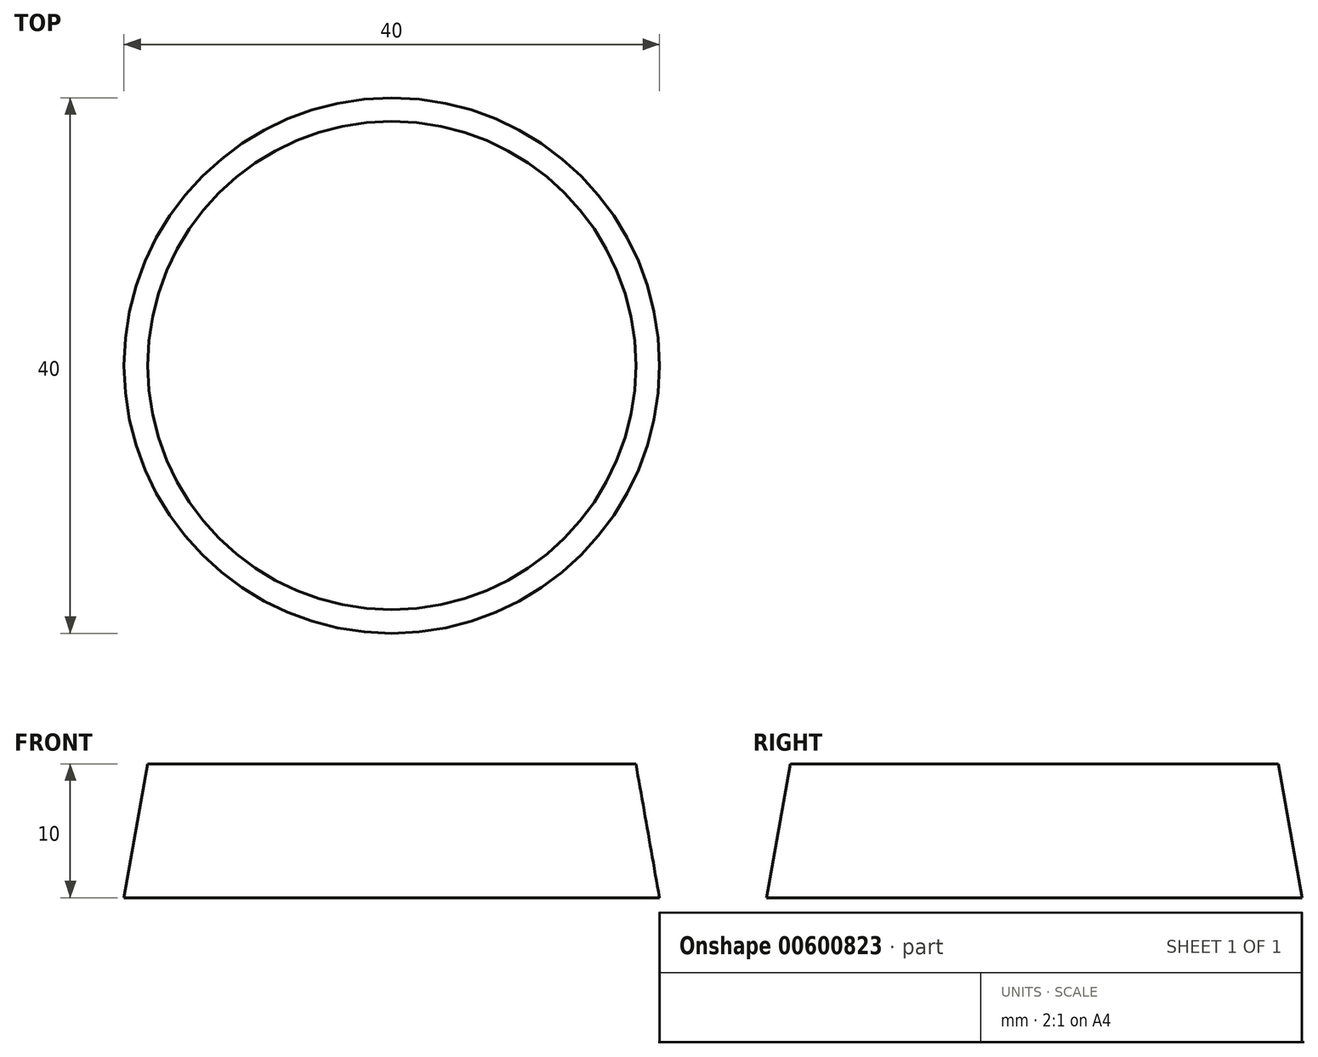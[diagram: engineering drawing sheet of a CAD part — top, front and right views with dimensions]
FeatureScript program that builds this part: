
annotation { "Feature Type Name" : "Feature", "Feature Type Description" : "" }
export const myFeature = defineFeature(function(context is Context, id is Id, definition is map)
    precondition{}
    {
        {
            var Q0;
            Q0=qCreatedBy(makeId("Top.planeOp"),FACE);
            var sketch = newSketch(context, id + "F0", { "sketchPlane" : qUnion([Q0])});
            skCircle(sketch, "E0", {"center": v(-16.9, 0) * mm, "radius": 20 * mm});
            skSolve(sketch);
        }
        {
            var Q0;
            Q0 = qSketchRegion(id + "F0", true);
            extrude(context, id + "F1", {"entities" : qUnion([Q0]), "depth" : 10 * mm, "offsetDistance" : 25 * mm, "hasDraft" : true, "draftAngle" : 10 * degree, "draftPullDirection" : true});
        }
    });
